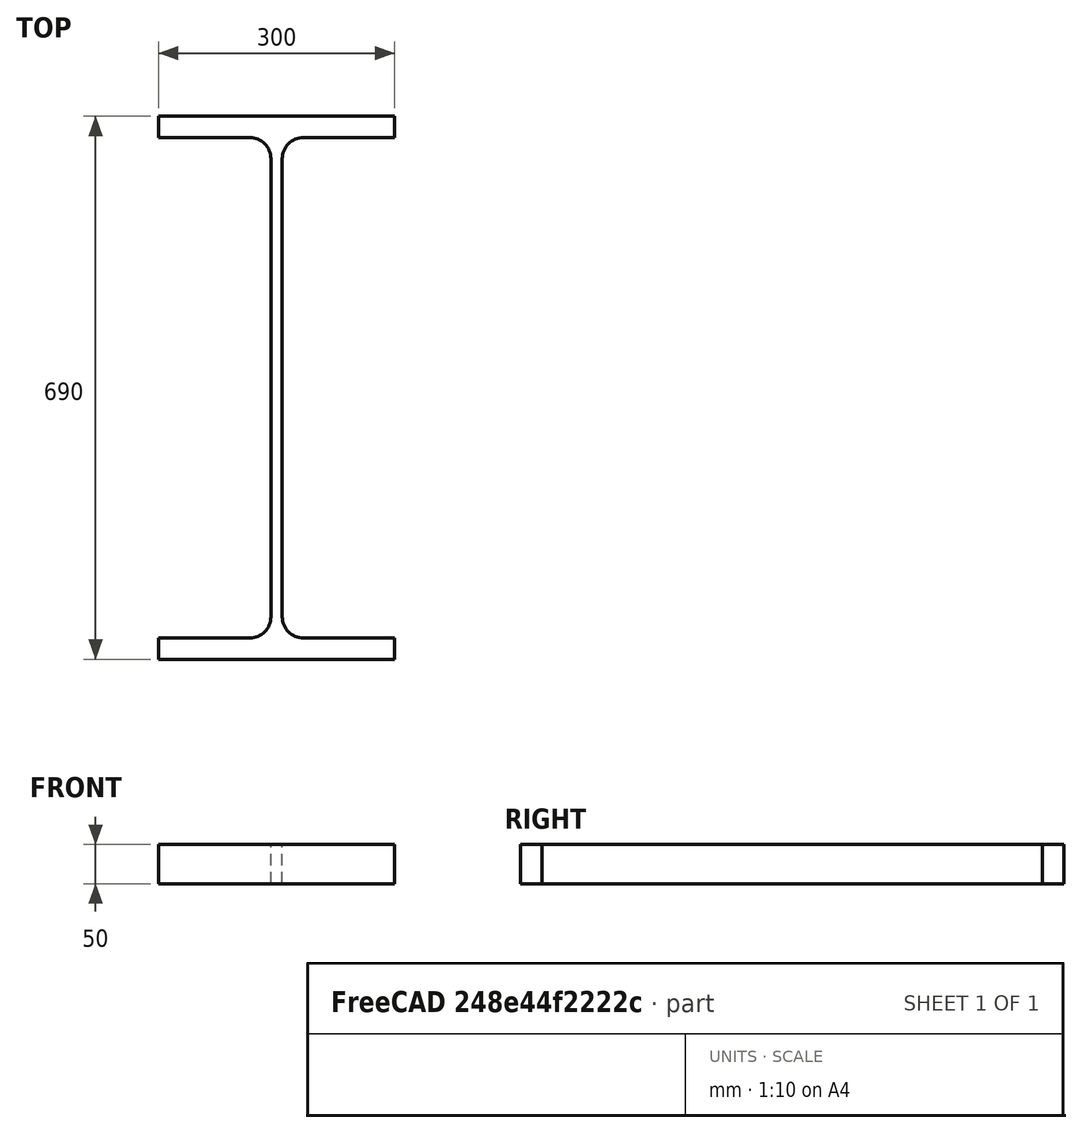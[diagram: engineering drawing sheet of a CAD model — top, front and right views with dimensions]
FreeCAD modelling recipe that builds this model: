
FCSTD DOCUMENT  (FreeCAD 0.15R4671 (Git))
Label: HE-A-Profile 700 DIN1025-3 S235JR
License: All rights reserved
LicenseURL: http://en.wikipedia.org/wiki/All_rights_reserved
objects: Sketcher::SketchObject×1, Part::Extrusion×1
note: 2 computed .brp shape members not serialized (recipe doc carries the construction recipe); baked Part::Feature solids carry a one-line shape summary decoded from their .brp

FEATURE [Sketcher::SketchObject] Sketch
  sketch-geometry (16):
    g0: LineSegment StartX=7.25 StartY=-291 StartZ=0 EndX=7.25 EndY=291 EndZ=0
    g1: LineSegment StartX=34.25 StartY=318 StartZ=0 EndX=150 EndY=318 EndZ=0
    g2: LineSegment StartX=150 StartY=318 StartZ=0 EndX=150 EndY=345 EndZ=0
    g3: LineSegment StartX=150 StartY=345 StartZ=0 EndX=-150 EndY=345 EndZ=0
    g4: LineSegment StartX=-150 StartY=345 StartZ=0 EndX=-150 EndY=318 EndZ=0
    g5: LineSegment StartX=-150 StartY=318 StartZ=0 EndX=-34.25 EndY=318 EndZ=0
    g6: LineSegment StartX=-7.25 StartY=291 StartZ=0 EndX=-7.25 EndY=-291 EndZ=0
    g7: LineSegment StartX=-34.25 StartY=-318 StartZ=0 EndX=-150 EndY=-318 EndZ=0
    g8: LineSegment StartX=-150 StartY=-318 StartZ=0 EndX=-150 EndY=-345 EndZ=0
    g9: LineSegment StartX=-150 StartY=-345 StartZ=0 EndX=150 EndY=-345 EndZ=0
    g10: LineSegment StartX=150 StartY=-345 StartZ=0 EndX=150 EndY=-318 EndZ=0
    g11: LineSegment StartX=150 StartY=-318 StartZ=0 EndX=34.25 EndY=-318 EndZ=0
    g12: ArcOfCircle CenterX=34.25 CenterY=291 CenterZ=0 NormalX=0 NormalY=0 NormalZ=1 Radius=27 StartAngle=1.5708 EndAngle=3.14159
    g13: ArcOfCircle CenterX=34.25 CenterY=-291 CenterZ=0 NormalX=0 NormalY=0 NormalZ=1 Radius=27 StartAngle=3.14159 EndAngle=4.71239
    g14: ArcOfCircle CenterX=-34.25 CenterY=291 CenterZ=0 NormalX=0 NormalY=0 NormalZ=1 Radius=27 StartAngle=0 EndAngle=1.5708
    g15: ArcOfCircle CenterX=-34.25 CenterY=-291 CenterZ=0 NormalX=0 NormalY=0 NormalZ=1 Radius=27 StartAngle=4.71239 EndAngle=6.28319
  constraints (42):
    c: Vertical(g0)
    c: Coincident(g2,g1)
    c: Vertical(g2)
    c: Coincident(g3,g2)
    c: Coincident(g4,g3)
    c: Vertical(g4)
    c: Coincident(g5,g4)
    c: Horizontal(g5)
    c: Vertical(g6)
    c: Horizontal(g7)
    c: Coincident(g8,g7)
    c: Vertical(g8)
    c: Coincident(g9,g8)
    c: Horizontal(g9)
    c: Coincident(g10,g9)
    c: Vertical(g10)
    c: Coincident(g11,g10)
    c: Horizontal(g11)
    c: Tangent(g1,g12) = 1.5708
    c: Tangent(g0,g12) = 1.5708
    c: Tangent(g0,g13) = 1.5708
    c: Tangent(g11,g13) = 1.5708
    c: Tangent(g5,g14) = 1.5708
    c: Tangent(g6,g14) = 1.5708
    c: Tangent(g6,g15) = 1.5708
    c: Tangent(g7,g15) = 1.5708
    c: Equal(g3,g9)
    c: Equal(g2,g4)
    c: Equal(g4,g8)
    c: Equal(g8,g10)
    c: Equal(g12,g14)
    c: Equal(g14,g15)
    c: Equal(g15,g13)
    c: Symmetric(g2,g3,g-2)
    c: Symmetric(g9,g8,g-2)
    c: Symmetric(g0,g6,g-2)
    c: Symmetric(g2,g9,g-1)
    c: DistanceY(g2,g9) = -690
    c: DistanceX(g3) = -300
    c: DistanceX(g0,g6) = -14.5
    c: DistanceY(g2) = 27
    c: Radius(g12) = 27
FEATURE [Part::Extrusion] Extrude  label="HE-A-Profile 700 DIN1025-3 S235JR"
  Base = -> Sketch
  Dir = (0,0,50)
  Solid = true
